# Revit family: 715-30-003-DN65-350
name_source: partatom
category: Pipe Accessories
units: mm (PartAtom-declared; Revit-internal decimal feet)

## family parameters
Always vertical = No
Cut with Voids When Loaded = No
Part Type = Valve - Breaks Into
Round Connector Dimension = Use Diameter
Shared = No
Work Plane-Based = No

## types (9) — shared parameters
Body_Wallthickness = 15 mm  [stored 0.0492126 ft]
DN065_PN10/16 = 715-065-30-03009
DN080_PN10/16 = 715-080-30-03009
DN100_PN10/16 = 715-100-30-03009
DN125_PN10/16 = 715-125-30-030099
DN150_PN10/16 = 715-150-30-03009
DN200_PN10 = 715-200-30-03009
DN250_PN10 = 715-250-30-03009
DN300_PN10 = 715-300-30-03009
DN350_PN10 = 715-350-30-03009
Description_ = AVK GATE VALVE, FLANGED, W/ACTUATOR
Fillet_Thickness_2 = 6 mm  [stored 0.019685 ft]
Ftc = 4 mm  [stored 0.0131234 ft]
Name_Height_reference = 10 mm  [stored 0.0328084 ft]
Rib_Thickness = 18 mm  [stored 0.0590551 ft]
Search_table = 715-30-003-DN65-350
URL product pages = https://www.avkvalves.com
zero-valued in all types: Bottom_Reference

## per-type parameters (varying)
- DN065_PN10/16: At=54 mm; Body_Height=130 mm; Body_depth=107 mm; Body_width=72 mm; Bolt_height=8 mm  [stored 0.0262467 ft]; Bolt_height_ref=235 mm; Bonnet_Flange_Depth=135 mm; Bonnet_Flange_Depth_ref=70 mm; Bonnet_Flange_Width=65 mm; Bonnet_Flange_Width_ref=20 mm  [stored 0.0656168 ft]; Bonnet_Flange_cut=8 mm  [stored 0.0262467 ft]; Bonnet_Flange_thickness=15 mm  [stored 0.0492126 ft]; Bonnet_Height=46 mm; Bonnet_Reference_height=140 mm; Bonnet_Thickness=73 mm; Bt=73 mm; Bt_2=66 mm; CL _Thickness=25 mm  [stored 0.082021 ft]; CL_Height=59 mm; Cut_Reference=340 mm; D=40 mm  [stored 0.131234 ft]; D1=10 mm  [stored 0.0328084 ft]; D2=61 mm; E=11 mm  [stored 0.0360892 ft]; F=10 mm  [stored 0.0328084 ft]; F1=20 mm  [stored 0.0656168 ft]; F2=34 mm  [stored 0.111549 ft]; Fillet_Thickness=6 mm  [stored 0.019685 ft]; Flange_OR=93 mm; Flange_Thickness=19 mm  [stored 0.062336 ft]; Flange_Thickness_cut=30 mm  [stored 0.0984252 ft]; Flange_Thickness_ref=38 mm  [stored 0.124672 ft]; Flange_Thickness_ref_2=57 mm; Ftc_reference_height=93 mm; H=585 mm; H1=548 mm; H1_ref=227 mm; H3=678 mm; H3_ref=371 mm; H_ref=288 mm; Horizontal_Flange_width=166 mm; ID (Radius)=33 mm; L=170 mm; L_Dia=65 mm; Name_Reference=96 mm; Name_Width=36 mm  [stored 0.11811 ft]; Neck_H=28 mm  [stored 0.0918635 ft]; Neck_T=23 mm  [stored 0.0754593 ft]; Neck_T2=21 mm; Nominal Diameter (DN)=65 mm; R1tv=925 mm; R2f=15 mm  [stored 0.0492126 ft]; RF_Dia=59 mm; Rf=277 mm; Rib_Height_Reference_1=120 mm; Rib_Height_Reference_2=110 mm; Rib_Height_Reference_3=100 mm; Rib_Height_Reference_4=75 mm; Rib_Width_1=36 mm  [stored 0.11811 ft]; Rib_Width_2=36 mm  [stored 0.11811 ft]; Rib_Width_3=36 mm  [stored 0.11811 ft]; Rib_depth_1=36 mm  [stored 0.11811 ft]; Rib_depth_2=36 mm  [stored 0.11811 ft]; Rib_depth_3=36 mm  [stored 0.11811 ft]; Rt=308 mm; Top_flange=45 mm  [stored 0.147638 ft]; Top_height_ref=74 mm; W=163 mm
- DN080_PN10/16: At=70 mm; Body_Height=135 mm; Body_depth=140 mm; Body_width=75 mm; Bolt_height=8 mm  [stored 0.0262467 ft]; Bolt_height_ref=255 mm; Bonnet_Flange_Depth=171 mm; Bonnet_Flange_Depth_ref=65 mm; Bonnet_Flange_Width=76 mm; Bonnet_Flange_Width_ref=22 mm  [stored 0.0721785 ft]; Bonnet_Flange_cut=8 mm  [stored 0.0262467 ft]; Bonnet_Flange_thickness=15 mm  [stored 0.0492126 ft]; Bonnet_Height=50 mm; Bonnet_Reference_height=145 mm; Bonnet_Thickness=77 mm; Bt=77 mm; Bt_2=69 mm; CL _Thickness=27 mm  [stored 0.0885827 ft]; CL_Height=75 mm; Cut_Reference=360 mm; D=40 mm  [stored 0.131234 ft]; D1=10 mm  [stored 0.0328084 ft]; D2=47 mm  [stored 0.154199 ft]; E=15 mm  [stored 0.0492126 ft]; F=10 mm  [stored 0.0328084 ft]; F1=20 mm  [stored 0.0656168 ft]; F2=34 mm  [stored 0.111549 ft]; Fillet_Thickness=6 mm  [stored 0.019685 ft]; Flange_OR=100 mm; Flange_Thickness=19 mm  [stored 0.062336 ft]; Flange_Thickness_cut=30 mm  [stored 0.0984252 ft]; Flange_Thickness_ref=38 mm  [stored 0.124672 ft]; Flange_Thickness_ref_2=57 mm; Ftc_reference_height=100 mm; H=560 mm; H1=523 mm; H1_ref=247 mm; H3=660 mm; H3_ref=384 mm; H_ref=294 mm; Horizontal_Flange_width=180 mm; ID (Radius)=40 mm  [stored 0.131234 ft]; L=180 mm; L_Dia=80 mm; Name_Reference=90 mm; Name_Width=38 mm  [stored 0.124672 ft]; Neck_H=22 mm  [stored 0.0721785 ft]; Neck_T=25 mm  [stored 0.082021 ft]; Neck_T2=23 mm  [stored 0.0754593 ft]; Nominal Diameter (DN)=80 mm; R1tv=1000 mm; R2f=15 mm  [stored 0.0492126 ft]; RF_Dia=66 mm; Rf=300 mm; Rib_Height_Reference_1=120 mm; Rib_Height_Reference_2=110 mm; Rib_Height_Reference_3=100 mm; Rib_Height_Reference_4=85 mm; Rib_Width_1=38 mm  [stored 0.124672 ft]; Rib_Width_2=38 mm  [stored 0.124672 ft]; Rib_Width_3=38 mm  [stored 0.124672 ft]; Rib_depth_1=38 mm  [stored 0.124672 ft]; Rib_depth_2=38 mm  [stored 0.124672 ft]; Rib_depth_3=38 mm  [stored 0.124672 ft]; Rt=333 mm; Top_flange=44 mm  [stored 0.144357 ft]; Top_height_ref=74 mm; W=163 mm
- DN100_PN10/16: At=83 mm; Body_Height=140 mm; Body_depth=166 mm; Body_width=80 mm; Bolt_height=10 mm  [stored 0.0328084 ft]; Bolt_height_ref=280 mm; Bonnet_Flange_Depth=192 mm; Bonnet_Flange_Depth_ref=70 mm; Bonnet_Flange_Width=81 mm; Bonnet_Flange_Width_ref=25 mm  [stored 0.082021 ft]; Bonnet_Flange_cut=8 mm  [stored 0.0262467 ft]; Bonnet_Flange_thickness=15 mm  [stored 0.0492126 ft]; Bonnet_Height=55 mm; Bonnet_Reference_height=150 mm; Bonnet_Thickness=82 mm; Bt=82 mm; Bt_2=74 mm; CL _Thickness=29 mm  [stored 0.0951444 ft]; CL_Height=88 mm; Cut_Reference=380 mm; D=50 mm; D1=10 mm  [stored 0.0328084 ft]; D2=54 mm; E=15 mm  [stored 0.0492126 ft]; F=10 mm  [stored 0.0328084 ft]; F1=22 mm  [stored 0.0721785 ft]; F2=34 mm  [stored 0.111549 ft]; Fillet_Thickness=6 mm  [stored 0.019685 ft]; Flange_OR=110 mm; Flange_Thickness=19 mm  [stored 0.062336 ft]; Flange_Thickness_cut=30 mm  [stored 0.0984252 ft]; Flange_Thickness_ref=38 mm  [stored 0.124672 ft]; Flange_Thickness_ref_2=57 mm; Ftc_reference_height=110 mm; H=594 mm; H1=557 mm; H1_ref=270 mm; H3=704 mm; H3_ref=421 mm; H_ref=324 mm; Horizontal_Flange_width=194 mm; ID (Radius)=50 mm; L=190 mm; L_Dia=100 mm; Name_Reference=101 mm; Name_Width=40 mm  [stored 0.131234 ft]; Neck_H=27 mm  [stored 0.0885827 ft]; Neck_T=27 mm  [stored 0.0885827 ft]; Neck_T2=25 mm  [stored 0.082021 ft]; Nominal Diameter (DN)=100 mm; R1tv=1100 mm; R2f=15 mm  [stored 0.0492126 ft]; RF_Dia=78 mm; Rf=323 mm; Rib_Height_Reference_1=120 mm; Rib_Height_Reference_2=110 mm; Rib_Height_Reference_3=100 mm; Rib_Height_Reference_4=90 mm; Rib_Width_1=40 mm  [stored 0.131234 ft]; Rib_Width_2=40 mm  [stored 0.131234 ft]; Rib_Width_3=40 mm  [stored 0.131234 ft]; Rib_depth_1=40 mm  [stored 0.131234 ft]; Rib_depth_2=40 mm  [stored 0.131234 ft]; Rib_depth_3=40 mm  [stored 0.131234 ft]; Rt=367 mm; Top_flange=48 mm  [stored 0.15748 ft]; Top_height_ref=74 mm; W=163 mm
- DN125_PN10/16: At=100 mm; Body_Height=165 mm; Body_depth=200 mm; Body_width=85 mm; Bolt_height=10 mm  [stored 0.0328084 ft]; Bolt_height_ref=330 mm; Bonnet_Flange_Depth=230 mm; Bonnet_Flange_Depth_ref=70 mm; Bonnet_Flange_Width=91 mm; Bonnet_Flange_Width_ref=25 mm  [stored 0.082021 ft]; Bonnet_Flange_cut=8 mm  [stored 0.0262467 ft]; Bonnet_Flange_thickness=15 mm  [stored 0.0492126 ft]; Bonnet_Height=63 mm; Bonnet_Reference_height=175 mm; Bonnet_Thickness=87 mm; Bt=87 mm; Bt_2=79 mm; CL _Thickness=32 mm  [stored 0.104987 ft]; CL_Height=105 mm; Cut_Reference=400 mm; D=50 mm; D1=10 mm  [stored 0.0328084 ft]; D2=60 mm; E=15 mm  [stored 0.0492126 ft]; F=10 mm  [stored 0.0328084 ft]; F1=22 mm  [stored 0.0721785 ft]; F2=34 mm  [stored 0.111549 ft]; Fillet_Thickness=6 mm  [stored 0.019685 ft]; Flange_OR=125 mm; Flange_Thickness=19 mm  [stored 0.062336 ft]; Flange_Thickness_cut=31 mm; Flange_Thickness_ref=38 mm  [stored 0.124672 ft]; Flange_Thickness_ref_2=57 mm; Ftc_reference_height=125 mm; H=604 mm; H1=586 mm; H1_ref=320 mm; H3=730 mm; H3_ref=500 mm; H_ref=380 mm; Horizontal_Flange_width=240 mm; ID (Radius)=63 mm; L=200 mm; L_Dia=125 mm; Name_Reference=123 mm; Name_Width=43 mm  [stored 0.141076 ft]; Neck_H=35 mm  [stored 0.114829 ft]; Neck_T=30 mm  [stored 0.0984252 ft]; Neck_T2=28 mm  [stored 0.0918635 ft]; Nominal Diameter (DN)=125 mm; R1tv=1250 mm; R2f=15 mm  [stored 0.0492126 ft]; RF_Dia=85 mm; Rf=400 mm; Rib_Height_Reference_1=120 mm; Rib_Height_Reference_2=110 mm; Rib_Height_Reference_3=100 mm; Rib_Height_Reference_4=120 mm; Rib_Width_1=43 mm  [stored 0.141076 ft]; Rib_Width_2=43 mm  [stored 0.141076 ft]; Rib_Width_3=43 mm  [stored 0.141076 ft]; Rib_depth_1=43 mm  [stored 0.141076 ft]; Rib_depth_2=43 mm  [stored 0.141076 ft]; Rib_depth_3=43 mm  [stored 0.141076 ft]; Rt=417 mm; Top_flange=48 mm  [stored 0.15748 ft]; Top_height_ref=114 mm; W=250 mm
- DN150_PN10/16: At=121 mm; Body_Height=180 mm; Body_depth=242 mm; Body_width=95 mm; Bolt_height=10 mm  [stored 0.0328084 ft]; Bolt_height_ref=375 mm; Bonnet_Flange_Depth=272 mm; Bonnet_Flange_Depth_ref=80 mm; Bonnet_Flange_Width=116 mm; Bonnet_Flange_Width_ref=30 mm  [stored 0.0984252 ft]; Bonnet_Flange_cut=8 mm  [stored 0.0262467 ft]; Bonnet_Flange_thickness=15 mm  [stored 0.0492126 ft]; Bonnet_Height=71 mm; Bonnet_Reference_height=190 mm; Bonnet_Thickness=97 mm; Bt=97 mm; Bt_2=89 mm; CL _Thickness=34 mm  [stored 0.111549 ft]; CL_Height=126 mm; Cut_Reference=420 mm; D=55 mm; D1=10 mm  [stored 0.0328084 ft]; D2=64 mm; E=15 mm  [stored 0.0492126 ft]; F=12 mm  [stored 0.0393701 ft]; F1=22 mm  [stored 0.0721785 ft]; F2=34 mm  [stored 0.111549 ft]; Fillet_Thickness=12 mm  [stored 0.0393701 ft]; Flange_OR=143 mm; Flange_Thickness=19 mm  [stored 0.062336 ft]; Flange_Thickness_cut=34 mm  [stored 0.111549 ft]; Flange_Thickness_ref=38 mm  [stored 0.124672 ft]; Flange_Thickness_ref_2=57 mm; Ftc_reference_height=143 mm; H=759 mm; H1=722 mm; H1_ref=365 mm; H3=902 mm; H3_ref=550 mm; H_ref=429 mm; Horizontal_Flange_width=242 mm; ID (Radius)=75 mm; L=210 mm; L_Dia=150 mm; Name_Reference=143 mm; Name_Width=48 mm  [stored 0.15748 ft]; Neck_H=44 mm  [stored 0.144357 ft]; Neck_T=32 mm  [stored 0.104987 ft]; Neck_T2=30 mm  [stored 0.0984252 ft]; Nominal Diameter (DN)=150 mm; R1tv=1425 mm; R2f=30 mm  [stored 0.0984252 ft]; RF_Dia=106 mm; Rf=403 mm; Rib_Height_Reference_1=120 mm; Rib_Height_Reference_2=110 mm; Rib_Height_Reference_3=100 mm; Rib_Height_Reference_4=150 mm; Rib_Width_1=48 mm  [stored 0.15748 ft]; Rib_Width_2=48 mm  [stored 0.15748 ft]; Rib_Width_3=48 mm  [stored 0.15748 ft]; Rib_depth_1=48 mm  [stored 0.15748 ft]; Rib_depth_2=48 mm  [stored 0.15748 ft]; Rib_depth_3=48 mm  [stored 0.15748 ft]; Rt=475 mm; Top_flange=55 mm; Top_height_ref=90 mm; W=199 mm
- DN200_PN10: At=160 mm; Body_Height=225 mm; Body_depth=320 mm; Body_width=108 mm; Bolt_height=12 mm  [stored 0.0393701 ft]; Bolt_height_ref=468 mm; Bonnet_Flange_Depth=332 mm; Bonnet_Flange_Depth_ref=85 mm; Bonnet_Flange_Width=132 mm; Bonnet_Flange_Width_ref=32 mm  [stored 0.104987 ft]; Bonnet_Flange_cut=13 mm; Bonnet_Flange_thickness=25 mm  [stored 0.082021 ft]; Bonnet_Height=85 mm; Bonnet_Reference_height=235 mm; Bonnet_Thickness=110 mm; Bt=110 mm; Bt_2=102 mm; CL _Thickness=34 mm  [stored 0.111549 ft]; CL_Height=165 mm; Cut_Reference=460 mm; D=63 mm; D1=10 mm  [stored 0.0328084 ft]; D2=75 mm; E=15 mm  [stored 0.0492126 ft]; F=14 mm  [stored 0.0459318 ft]; F1=28 mm  [stored 0.0918635 ft]; F2=34 mm  [stored 0.111549 ft]; Fillet_Thickness=24 mm  [stored 0.0787402 ft]; Flange_OR=170 mm; Flange_Thickness=20 mm  [stored 0.0656168 ft]; Flange_Thickness_cut=35 mm  [stored 0.114829 ft]; Flange_Thickness_ref=40 mm  [stored 0.131234 ft]; Flange_Thickness_ref_2=60 mm; Ftc_reference_height=170 mm; H=948 mm; H1=911 mm; H1_ref=456 mm; H3=1118 mm; H3_ref=677 mm; H_ref=531 mm; Horizontal_Flange_width=292 mm; ID (Radius)=100 mm; L=230 mm; L_Dia=200 mm; Name_Reference=183 mm; Name_Width=54 mm; Neck_H=51 mm; Neck_T=32 mm  [stored 0.104987 ft]; Neck_T2=30 mm  [stored 0.0984252 ft]; Nominal Diameter (DN)=200 mm; R1tv=1700 mm; R2f=60 mm; RF_Dia=133 mm; Rf=487 mm; Rib_Height_Reference_1=120 mm; Rib_Height_Reference_2=110 mm; Rib_Height_Reference_3=100 mm; Rib_Height_Reference_4=180 mm; Rib_Width_1=54 mm; Rib_Width_2=54 mm; Rib_Width_3=54 mm; Rib_depth_1=54 mm; Rib_depth_2=54 mm; Rib_depth_3=54 mm; Rt=567 mm; Top_flange=59 mm; Top_height_ref=123 mm; W=271 mm
- DN250_PN10: At=185 mm; Body_Height=275 mm; Body_depth=370 mm; Body_width=124 mm; Bolt_height=12 mm  [stored 0.0393701 ft]; Bolt_height_ref=527 mm; Bonnet_Flange_Depth=372 mm; Bonnet_Flange_Depth_ref=100 mm; Bonnet_Flange_Width=158 mm; Bonnet_Flange_Width_ref=40 mm  [stored 0.131234 ft]; Bonnet_Flange_cut=13 mm; Bonnet_Flange_thickness=25 mm  [stored 0.082021 ft]; Bonnet_Height=100 mm; Bonnet_Reference_height=285 mm; Bonnet_Thickness=126 mm; Bt=126 mm; Bt_2=118 mm; CL _Thickness=42 mm  [stored 0.137795 ft]; CL_Height=190 mm; Cut_Reference=500 mm; D=88 mm; D1=15 mm  [stored 0.0492126 ft]; D2=99 mm; E=13 mm; F=14 mm  [stored 0.0459318 ft]; F1=27 mm  [stored 0.0885827 ft]; F2=47 mm  [stored 0.154199 ft]; Fillet_Thickness=24 mm  [stored 0.0787402 ft]; Flange_OR=200 mm; Flange_Thickness=22 mm  [stored 0.0721785 ft]; Flange_Thickness_cut=38 mm  [stored 0.124672 ft]; Flange_Thickness_ref=44 mm  [stored 0.144357 ft]; Flange_Thickness_ref_2=66 mm; Ftc_reference_height=200 mm; H=1088 mm; H1=1051 mm; H1_ref=515 mm; H3=1288 mm; H3_ref=817 mm; H_ref=614 mm; Horizontal_Flange_width=406 mm; ID (Radius)=125 mm; L=250 mm; L_Dia=250 mm; Name_Reference=270 mm; Name_Width=62 mm; Neck_H=37 mm  [stored 0.121391 ft]; Neck_T=40 mm  [stored 0.131234 ft]; Neck_T2=38 mm  [stored 0.124672 ft]; Nominal Diameter (DN)=250 mm; R1tv=2000 mm; R2f=60 mm; RF_Dia=160 mm; Rf=677 mm; Rib_Height_Reference_1=90 mm; Rib_Height_Reference_2=110 mm; Rib_Height_Reference_3=100 mm; Rib_Height_Reference_4=200 mm; Rib_Width_1=150 mm; Rib_Width_2=150 mm; Rib_Width_3=62 mm; Rib_depth_1=385 mm; Rib_depth_2=62 mm; Rib_depth_3=62 mm; Rt=667 mm; Top_flange=70 mm; Top_height_ref=172 mm; W=378 mm
- DN300_PN10: At=209 mm; Body_Height=330 mm; Body_depth=418 mm; Body_width=157 mm; Bolt_height=14 mm  [stored 0.0459318 ft]; Bolt_height_ref=624 mm; Bonnet_Flange_Depth=432 mm; Bonnet_Flange_Depth_ref=140 mm; Bonnet_Flange_Width=206 mm; Bonnet_Flange_Width_ref=50 mm; Bonnet_Flange_cut=18 mm  [stored 0.0590551 ft]; Bonnet_Flange_thickness=35 mm  [stored 0.114829 ft]; Bonnet_Height=114 mm; Bonnet_Reference_height=340 mm; Bonnet_Thickness=160 mm; Bt=160 mm; Bt_2=151 mm; CL _Thickness=59 mm; CL_Height=214 mm; Cut_Reference=540 mm; D=88 mm; D1=15 mm  [stored 0.0492126 ft]; D2=80 mm; E=13 mm; F=14 mm  [stored 0.0459318 ft]; F1=27 mm  [stored 0.0885827 ft]; F2=47 mm  [stored 0.154199 ft]; Fillet_Thickness=24 mm  [stored 0.0787402 ft]; Flange_OR=228 mm; Flange_Thickness=25 mm  [stored 0.082021 ft]; Flange_Thickness_cut=39 mm  [stored 0.127953 ft]; Flange_Thickness_ref=49 mm; Flange_Thickness_ref_2=74 mm; Ftc_reference_height=228 mm; H=1214 mm; H1=1177 mm; H1_ref=610 mm; H3=1442 mm; H3_ref=919 mm; H_ref=690 mm; Horizontal_Flange_width=458 mm; ID (Radius)=150 mm; L=270 mm; L_Dia=300 mm; Name_Reference=250 mm; Name_Width=79 mm; Neck_H=53 mm; Neck_T=57 mm; Neck_T2=55 mm; Nominal Diameter (DN)=300 mm; R1tv=2275 mm; R2f=60 mm; RF_Dia=185 mm; Rf=763 mm; Rib_Height_Reference_1=178 mm; Rib_Height_Reference_2=285 mm; Rib_Height_Reference_3=150 mm; Rib_Height_Reference_4=260 mm; Rib_Width_1=175 mm; Rib_Width_2=175 mm; Rib_Width_3=79 mm; Rib_depth_1=450 mm; Rib_depth_2=450 mm; Rib_depth_3=79 mm; Rt=758 mm; Top_flange=95 mm; Top_height_ref=172 mm; W=378 mm
- DN350_PN10: At=250 mm; Body_Height=410 mm; Body_depth=500 mm; Body_width=170 mm; Bolt_height=14 mm  [stored 0.0459318 ft]; Bolt_height_ref=749 mm; Bonnet_Flange_Depth=554 mm; Bonnet_Flange_Depth_ref=160 mm; Bonnet_Flange_Width=180 mm; Bonnet_Flange_Width_ref=55 mm; Bonnet_Flange_cut=18 mm  [stored 0.0590551 ft]; Bonnet_Flange_thickness=35 mm  [stored 0.114829 ft]; Bonnet_Height=130 mm; Bonnet_Reference_height=420 mm; Bonnet_Thickness=173 mm; Bt=173 mm; Bt_2=164 mm; CL _Thickness=65 mm; CL_Height=255 mm; Cut_Reference=580 mm; D=110 mm; D1=15 mm  [stored 0.0492126 ft]; D2=79 mm; E=28 mm  [stored 0.0918635 ft]; F=16 mm  [stored 0.0524934 ft]; F1=37 mm  [stored 0.121391 ft]; F2=55 mm; Fillet_Thickness=24 mm  [stored 0.0787402 ft]; Flange_OR=260 mm; Flange_Thickness=27 mm  [stored 0.0885827 ft]; Flange_Thickness_cut=43 mm  [stored 0.141076 ft]; Flange_Thickness_ref=53 mm; Flange_Thickness_ref_2=80 mm; Ftc_reference_height=260 mm; H=1429 mm; H1=1392 mm; H1_ref=735 mm; H3=1689 mm; H3_ref=1221 mm; H_ref=814 mm; Horizontal_Flange_width=814 mm; ID (Radius)=175 mm; L=290 mm; L_Dia=350 mm; Name_Reference=380 mm; Name_Width=85 mm; Neck_H=42 mm  [stored 0.137795 ft]; Neck_T=63 mm; Neck_T2=61 mm; Nominal Diameter (DN)=350 mm; R1tv=2600 mm; R2f=60 mm; RF_Dia=215 mm; Rf=1357 mm; Rib_Height_Reference_1=70 mm; Rib_Height_Reference_2=185 mm; Rib_Height_Reference_3=305 mm; Rib_Height_Reference_4=390 mm; Rib_Width_1=190 mm; Rib_Width_2=190 mm; Rib_Width_3=190 mm; Rib_depth_1=560 mm; Rib_depth_2=560 mm; Rib_depth_3=560 mm; Rt=867 mm; Top_flange=108 mm; Top_height_ref=172 mm; W=378 mm

note: [stored X ft] marks values corroborated as IEEE doubles in the binary element streams (Revit-internal decimal feet)

## geometry (parser evidence)
native form markers: Sweep x3
no freeform markers — native parametric forms only
